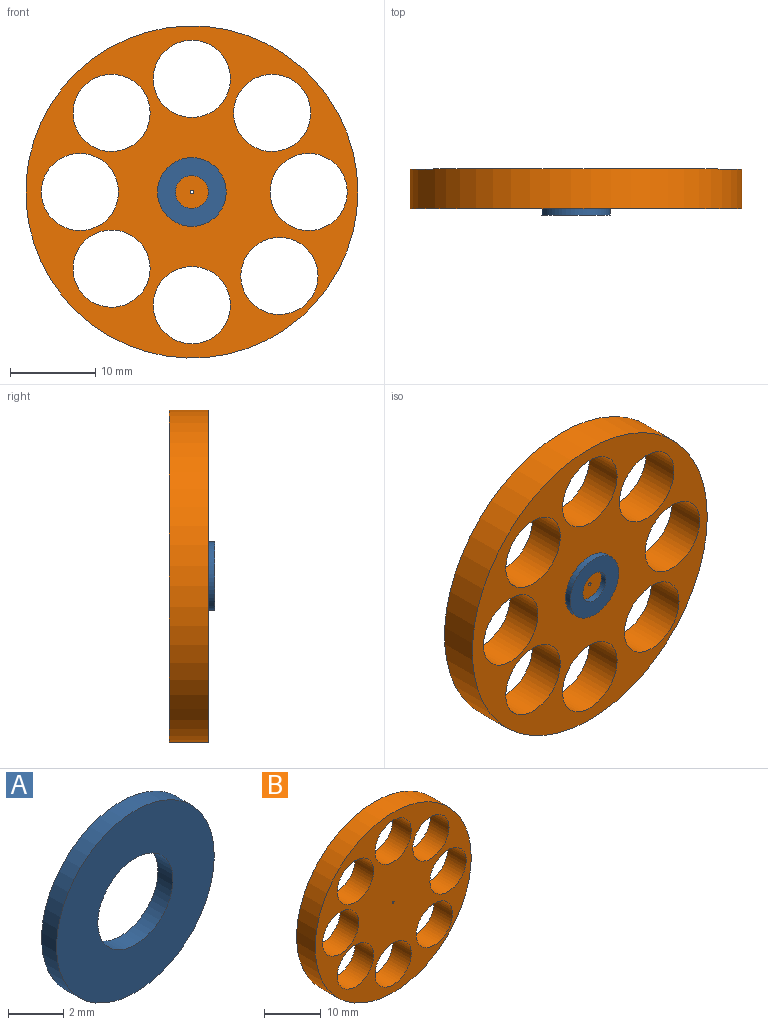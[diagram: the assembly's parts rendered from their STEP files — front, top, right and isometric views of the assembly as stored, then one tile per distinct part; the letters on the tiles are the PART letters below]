
ASSEMBLY  parts=2 mates=1
PART A: 4 faces, bbox 8.1x0.8x8.1 mm
  f0: cylinder r=1.92mm len=3.84mm, axis (0,1,0), area 9.2mm2, adj f1,f2
  f1: plane 8.05x8.05mm, normal (0,-1,0), area 39.4mm2, adj f0,f3
  f2: plane 8.05x8.05mm, normal (0,1,0), area 39.4mm2, adj f0,f3
  f3: cylinder r=4.03mm len=8.05mm, axis (0,1,0), area 19.3mm2, adj f1,f2
PART B: 12 faces, bbox 38.9x4.6x38.9 mm
  f0: cylinder r=0.2mm len=4.62mm, axis (0,1,0), area 5.9mm2, adj f9,f10
  f1: cylinder r=4.52mm len=9.04mm, axis (0,1,0), area 131.3mm2, adj f9,f10
  f2: cylinder r=4.52mm len=9.04mm, axis (0,1,0), area 131.3mm2, adj f9,f10
  f3: cylinder r=4.52mm len=9.04mm, axis (0,1,0), area 131.3mm2, adj f9,f10
  f4: cylinder r=4.52mm len=9.04mm, axis (0,1,0), area 131.3mm2, adj f9,f10
  f5: cylinder r=4.52mm len=9.04mm, axis (0,1,0), area 131.3mm2, adj f9,f10
  f6: cylinder r=4.52mm len=9.04mm, axis (0,1,0), area 131.3mm2, adj f9,f10
  f7: cylinder r=4.52mm len=9.04mm, axis (0,1,0), area 131.3mm2, adj f9,f10
  f8: cylinder r=4.52mm len=9.04mm, axis (0,1,0), area 131.3mm2, adj f9,f10
  f9: plane 38.94x38.94mm, normal (0,-1,0), area 676.9mm2, adj f0,f1,f2,f3,f4,f5,f6,f7
  f10: plane 38.94x38.94mm, normal (0,1,0), area 676.9mm2, adj f0,f1,f2,f3,f4,f5,f6,f7
  f11: cylinder r=19.47mm len=38.94mm, axis (0,1,0), area 565.5mm2, adj f9,f10
PLACE A t=(-5.33,4.63,15.03)mm
PLACE B t=(-5.33,5.39,15.03)mm
MATE revolute B.f0 <-> A.f0  axis (0,-1,0) through (-5.33,5.39,15.03)mm
